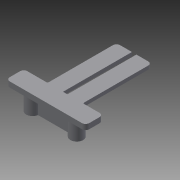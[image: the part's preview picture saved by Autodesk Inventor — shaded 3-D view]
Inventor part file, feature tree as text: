
AUTODESK INVENTOR PART (.ipt)
format: ipt  version: 2015 (Build 190159000, 159)  size: 159,744 bytes
history: native  units: mm
features: extrude x6, sketch x6, fillet x2
ambient origin geometry x8: Origin, YZ Plane, XZ Plane, XY Plane, X Axis, Y Axis, Z Axis, Center Point
bodies: Solid1 (feature_tree)
feature tree (14):
  extrude  "Extrusion1"  Depth=10.0mm
  extrude  "Extrusion2"  Depth=12.5mm
  extrude  "Extrusion3"  Depth=45.0mm
  extrude  "Extrusion4"  Depth=10.0mm
  fillet  "Fillet1"  Radius=10.0mm
  fillet  "Fillet2"  Radius=25.0mm
  extrude  "Extrusion5"  Depth=5.0mm
  extrude  "Extrusion6"  Depth=2.0mm TaperAngle=0.0deg
  sketch  "Sketch1"  dims[d0=20.0mm d1=10.0mm]
  sketch  "Sketch2"  dims[d2=40.0mm d3=12.5mm]
  sketch  "Sketch3"  dims[d4=12.5mm d5=45.0mm]
  sketch  "Sketch4"  dims[d6=2.0mm d7=0.0mm d8=5.2mm d9=10.0mm d10=25.0mm]
  sketch  "Sketch5"  dims[d11=5.2mm d12=5.0mm]
  sketch  "Sketch6"  dims[d13=5.0mm d14=2.0mm d15=0.0mm d16=1.0mm d17=0.0mm d18=2.5mm d19=40.0mm d20=8.75mm d21=8.75mm d22=2.0mm d23=0.0mm d24=2.0mm d25=2.0mm d26=7.2mm d27=7.2mm d28=10.0mm d29=0.0mm d30=0.5mm d31=0.5mm d32=10.0mm d33=0.0mm]
